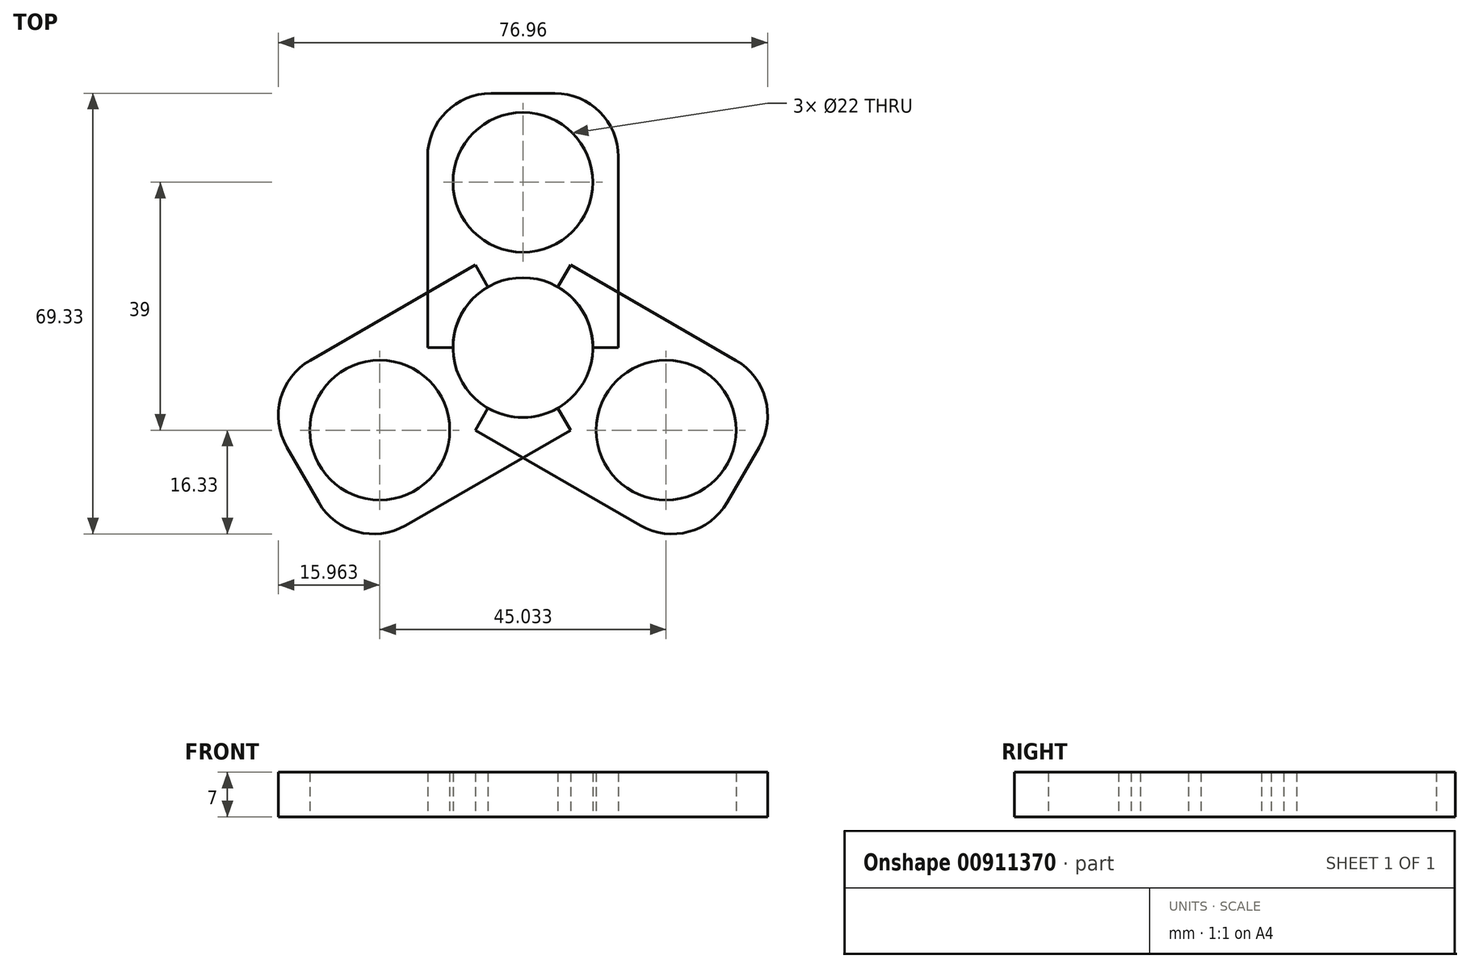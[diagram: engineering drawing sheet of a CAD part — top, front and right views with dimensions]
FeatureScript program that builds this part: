
annotation { "Feature Type Name" : "Feature", "Feature Type Description" : "" }
export const myFeature = defineFeature(function(context is Context, id is Id, definition is map)
    precondition{}
    {
        {
            var Q0;
            Q0=qCreatedBy(makeId("Top.planeOp"),FACE);
            var sketch = newSketch(context, id + "F0", { "sketchPlane" : qUnion([Q0])});
            skCircle(sketch, "E0", {"center": v(0, 0) * mm, "radius": 11 * mm});
            skLineSegment(sketch, "E1.bottom", {"start": v(0, 0) * mm, "end": v(15, 0) * mm});
            skLineSegment(sketch, "E1.top", {"start": v(0, 40) * mm, "end": v(5, 40) * mm});
            skLineSegment(sketch, "E1.left", {"start": v(0, 0) * mm, "end": v(0, 40) * mm});
            skLineSegment(sketch, "E1.right", {"start": v(15, 0) * mm, "end": v(15, 30) * mm});
            skLineSegment(sketch, "E2.bottom", {"start": v(0, 0) * mm, "end": v(-15, 0) * mm});
            skLineSegment(sketch, "E2.top", {"start": v(0, 40) * mm, "end": v(-5, 40) * mm});
            skLineSegment(sketch, "E2.right", {"start": v(-15, 0) * mm, "end": v(-15, 30) * mm});
            skLineSegment(sketch, "E3", {"start": v(0, 40) * mm, "end": v(0, 26) * mm});
            skCircle(sketch, "E4", {"center": v(0, 26) * mm, "radius": 11 * mm});
            skPoint(sketch, "E5.visualSharp", {"position": v(-15, 40) * mm});
            skArc(sketch, "E5.filletArc", {"start": v(-5, 40) * mm, "mid": v(-12.07, 37.07) * mm, "end": v(-15, 30) * mm});
            skPoint(sketch, "E6.visualSharp", {"position": v(15, 40) * mm});
            skArc(sketch, "E6.filletArc", {"start": v(15, 30) * mm, "mid": v(12.07, 37.07) * mm, "end": v(5, 40) * mm});
            skSolve(sketch);
        }
        {
            var Q0;
            {var subQ0=sQuery(id+"F0.wireOp",EDGE,"E2.top");Q0=makeQuery(id+"F0.imprint","IMPRINT",FACE,{"disambiguationData":[TD([[makeQuery(id+"F0.imprint","IMPRINT",EDGE,{"derivedFrom":subQ0}),1.0]])]});}
            var Q1;
            {var subQ9=sQuery(id+"F0.wireOp",EDGE,"E1.top");Q1=makeQuery(id+"F0.imprint","IMPRINT",FACE,{"disambiguationData":[TD([[makeQuery(id+"F0.imprint","IMPRINT",EDGE,{"derivedFrom":subQ9}),-1.0]])]});}
            var Q2;
            {var subQ0=sQuery(id+"F0.wireOp",EDGE,"E2.right");var subQ1=sQuery(id+"F0.wireOp",EDGE,"E2.bottom");var subQ2=makeQuery(id+"F0.imprint","INTERSECT",VERTEX,{"derivedFrom":[subQ1,subQ0]});Q2=makeQuery(id+"F0.imprint","IMPRINT",FACE,{"disambiguationData":[TD([[makeQuery(id+"F0.imprint","IMPRINT",EDGE,{"disambiguationData":[TD([[subQ2,1.0]])],"derivedFrom":subQ1}),-1.0]])]});}
            extrude(context, id + "F1", {"entities" : qUnion([Q0, Q1, Q2]), "depth" : 7 * mm, "offsetDistance" : 25 * mm});
        }
        {
            var Q0;
            Q0=qCreatedBy(makeId("Front.planeOp"),FACE);
            var sketch = newSketch(context, id + "F2", { "sketchPlane" : qUnion([Q0])});
            skLineSegment(sketch, "E7", {"start": v(0, 0) * mm, "end": v(0, 62.65) * mm});
            skSolve(sketch);
        }
        {
            var Q0;
            Q0=makeQuery(id+"F1.opExtrude","SWEPT_BODY",BODY,{"disambiguationData":[OSD([sQuery(id+"F0.wireOp",EDGE,"E0"),sQuery(id+"F0.wireOp",EDGE,"E1.bottom"),sQuery(id+"F0.wireOp",EDGE,"E1.top"),sQuery(id+"F0.wireOp",EDGE,"E1.right"),sQuery(id+"F0.wireOp",EDGE,"E2.bottom"),sQuery(id+"F0.wireOp",EDGE,"E2.top"),sQuery(id+"F0.wireOp",EDGE,"E2.right"),sQuery(id+"F0.wireOp",EDGE,"E4")])]});
            var Q1;
            Q1=sQuery(id+"F2.wireOp",EDGE,"E7");
            transform(context, id + "F3", {"entities" : qUnion([Q0]), "transformType" : TransformType.ROTATION, "transformAxis" : qUnion([Q1]), "angle" : 120 * degree, "makeCopy" : true});
        }
        {
            var Q0;
            Q0=makeQuery(id+"F3.opPattern","COPY",BODY,{"derivedFrom":makeQuery(id+"F1.opExtrude","SWEPT_BODY",BODY,{"disambiguationData":[OSD([sQuery(id+"F0.wireOp",EDGE,"E0"),sQuery(id+"F0.wireOp",EDGE,"E1.bottom"),sQuery(id+"F0.wireOp",EDGE,"E1.top"),sQuery(id+"F0.wireOp",EDGE,"E1.right"),sQuery(id+"F0.wireOp",EDGE,"E2.bottom"),sQuery(id+"F0.wireOp",EDGE,"E2.top"),sQuery(id+"F0.wireOp",EDGE,"E2.right"),sQuery(id+"F0.wireOp",EDGE,"E4")])]}),"instanceName":"1"});
            var Q1;
            Q1=sQuery(id+"F2.wireOp",EDGE,"E7");
            transform(context, id + "F4", {"entities" : qUnion([Q0]), "transformType" : TransformType.ROTATION, "transformAxis" : qUnion([Q1]), "angle" : 120 * degree, "makeCopy" : true});
        }
    });
